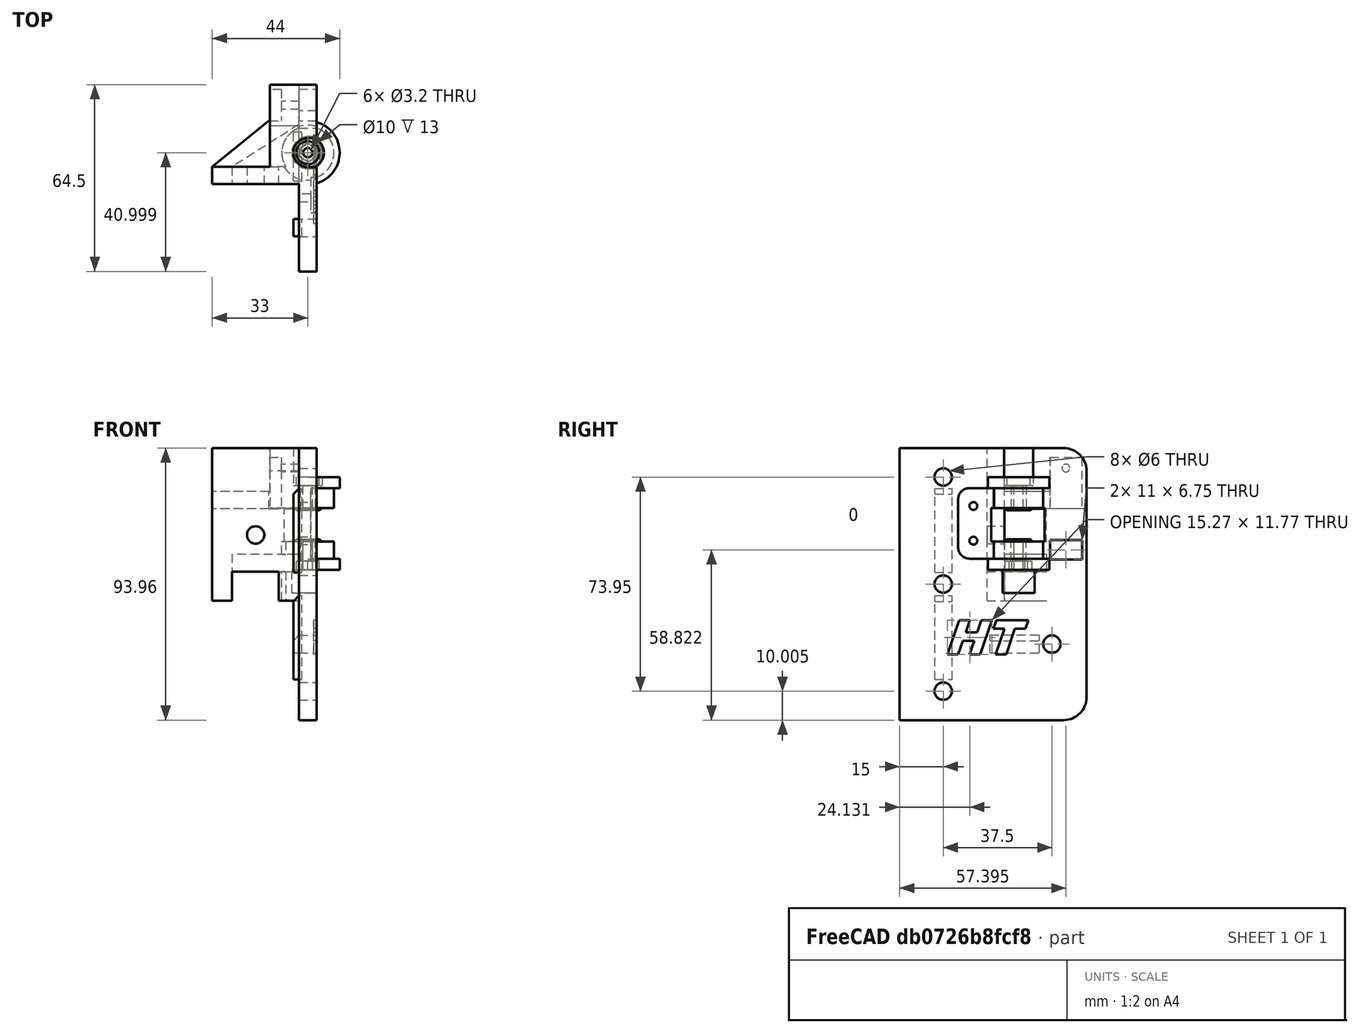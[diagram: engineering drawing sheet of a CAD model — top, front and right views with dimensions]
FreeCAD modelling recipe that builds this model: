
FCSTD DOCUMENT  (FreeCAD 0.18R16146 (Git))
Label: front-idler-right
License: All rights reserved
LicenseURL: http://en.wikipedia.org/wiki/All_rights_reserved
objects: Part::Cylinder×9, Part::Cut×6, Part::Chamfer×5, Part::Feature×4, Part::MultiFuse×4, Part::Box×3
note: 31 computed .brp shape members not serialized (recipe doc carries the construction recipe); baked Part::Feature solids carry a one-line shape summary decoded from their .brp

FEATURE [Part::Feature] Part__Feature  label="PulleyMount_FRONT_RIGHT_BodyV1.1"
  Placement = pos=(-440,-2.64,-417.58) rot=(1,0,0;1.5708rad)
  shape: bbox 44.04 x 64.54 x 93.99 mm, 115 faces (baked)
FEATURE [Part::Box] Box  label="Cube"
  AttacherType = Attacher::AttachEngine3D
  Height = 29
  Length = 3
  Placement = pos=(8,-8,14) rot=(0,0,1;0rad)
  Width = 6
FEATURE [Part::Box] Box001  label="Cube001"
  AttacherType = Attacher::AttachEngine3D
  Height = 29
  Length = 3
  Placement = pos=(8,-8,51) rot=(0,0,1;0rad)
  Width = 6
FEATURE [Part::Chamfer] Chamfer
  Base = -> Box001
  Edges = 1 edges r=2: [Edge2]
FEATURE [Part::Chamfer] Chamfer001
  Base = -> Box
  Edges = 1 edges r=2: [Edge2]
FEATURE [Part::Box] Box002  label="Cube002"
  AttacherType = Attacher::AttachEngine3D
  Height = 6.2
  Length = 3
  Placement = pos=(8,11,23.24) rot=(0,0,1;0rad)
  Width = 17
FEATURE [Part::Chamfer] Chamfer002
  Base = -> Box002
  Edges = 1 edges r=2: [Edge2]
FEATURE [Part::Feature] Part__Feature001  label="PulleyMount_FRONT_RIGHT_BodyV1.002"
  shape: bbox 44.04 x 64.54 x 93.99 mm, 115 faces (baked)
FEATURE [Part::MultiFuse] Fusion
  Shapes = -> [Chamfer,Chamfer002,Chamfer001]
FEATURE [Part::Cylinder] Cylinder  label="pos"
  Angle = 360
  AttacherType = Attacher::AttachEngine3D
  Height = 10
  Placement = pos=(13,20.8587,51.95) rot=(0,0,1;0rad)
  Radius = 1.6
FEATURE [Part::Cylinder] Cylinder001  label="pos001"
  Angle = 360
  AttacherType = Attacher::AttachEngine3D
  Height = 9.75
  Placement = pos=(13,20.8587,51.95) rot=(0,0,1;0rad)
  Radius = 5.55
FEATURE [Part::Cylinder] Cylinder002  label="pos002"
  Angle = 360
  AttacherType = Attacher::AttachEngine3D
  Height = 2
  Placement = pos=(13,20.8587,61.7) rot=(0,0,1;0rad)
  Radius = 6.55
FEATURE [Part::Cylinder] Cylinder003  label="pos003"
  Angle = 360
  AttacherType = Attacher::AttachEngine3D
  Height = 2
  Placement = pos=(13,20.8587,71.19) rot=(0,0,1;0rad)
  Radius = 6.55
FEATURE [Part::Cut] Cut
  Base = -> Part__Feature001
  Tool = -> Cylinder003
FEATURE [Part::Cut] Cut001
  Base = -> Cut
  Tool = -> Cylinder002
FEATURE [Part::Cylinder] Cylinder004  label="pos004"
  Angle = 360
  AttacherType = Attacher::AttachEngine3D
  Height = 10.75
  Placement = pos=(13,20.8587,73.2) rot=(0,0,1;0rad)
  Radius = 5.55
FEATURE [Part::MultiFuse] Fusion001
  Shapes = -> [Cut001,Cylinder004]
FEATURE [Part::Feature] Pad001
  Placement = pos=(13,20.86,51.95) rot=(0,0,1;0rad)
  shape: bbox 5.543 x 6.4 x 3 mm, 8 faces (baked)
FEATURE [Part::MultiFuse] Fusion002
  Shapes = -> [Fusion001,Cylinder001]
FEATURE [Part::Cut] Cut002
  Base = -> Fusion002
  Tool = -> Pad001
FEATURE [Part::Cylinder] Cylinder005  label="pos005"
  Angle = 360
  AttacherType = Attacher::AttachEngine3D
  Height = 35
  Placement = pos=(13,20.8587,51.95) rot=(0,0,1;0rad)
  Radius = 1.6
FEATURE [Part::Cut] Cut003
  Base = -> Cut002
  Tool = -> Cylinder005
FEATURE [Part::Cylinder] Cylinder006  label="pos006"
  Angle = 360
  AttacherType = Attacher::AttachEngine3D
  Height = 3
  Placement = pos=(13,20.8587,80.95) rot=(0,0,1;0rad)
  Radius = 4
FEATURE [Part::Cut] Cut004
  Base = -> Cut003
  Tool = -> Cylinder006
FEATURE [Part::Cylinder] Cylinder007  label="pos007"
  Angle = 360
  AttacherType = Attacher::AttachEngine3D
  Height = 0.75
  Placement = pos=(13,20.8587,129.95) rot=(0,0,1;0rad)
  Radius = 3.5
FEATURE [Part::Cylinder] Cylinder008  label="pos008"
  Angle = 360
  AttacherType = Attacher::AttachEngine3D
  Height = 0.75
  Placement = pos=(13,20.8587,129.95) rot=(0,0,1;0rad)
  Radius = 1.6
FEATURE [Part::Cut] Cut005
  Base = -> Cylinder007
  Placement = pos=(0,0,-68.25) rot=(0,0,1;0rad)
  Tool = -> Cylinder008
FEATURE [Part::Feature] Cut005001  label="Cut006"
  Placement = pos=(0,0,-57.51) rot=(0,0,1;0rad)
  shape: bbox 7 x 7 x 0.75 mm, 4 faces (baked)
FEATURE [Part::Chamfer] Chamfer003
  Base = -> Cut005001
  Edges = 1 edges r=0.5: [Edge3]
  Placement = pos=(0,0,0.1) rot=(0,0,1;0rad)
FEATURE [Part::Chamfer] Chamfer004
  Base = -> Cut005
  Edges = 1 edges r=0.5: [Edge1]
  Placement = pos=(0,0,-0.1) rot=(0,0,1;0rad)
FEATURE [Part::MultiFuse] Fusion003
  Shapes = -> [Cut004,Chamfer003,Chamfer004]
